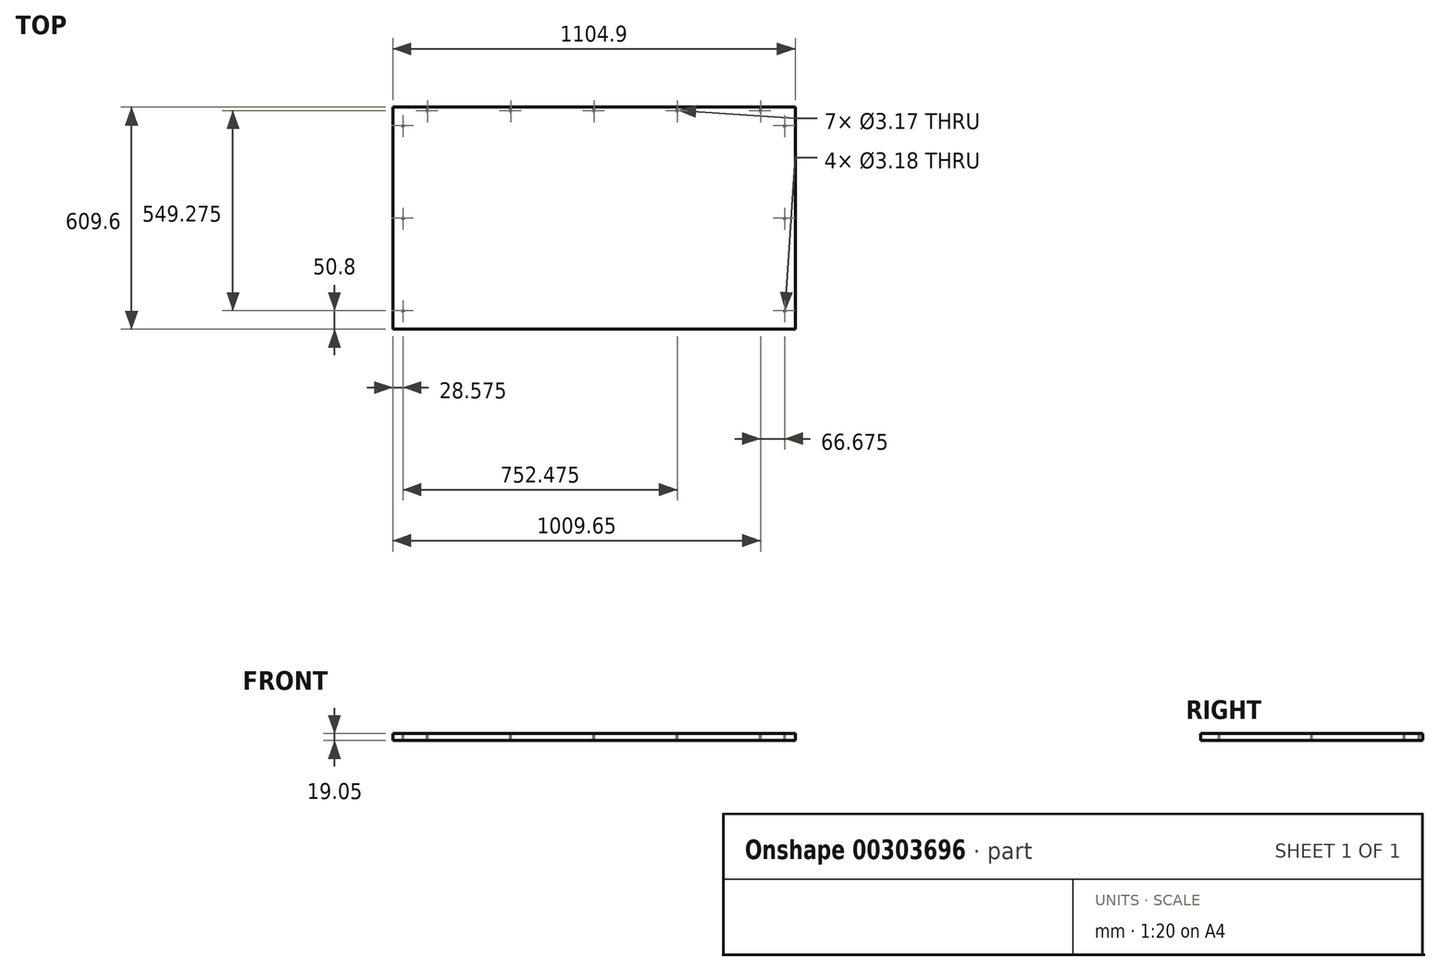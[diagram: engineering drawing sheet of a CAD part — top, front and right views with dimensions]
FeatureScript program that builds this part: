
annotation { "Feature Type Name" : "Feature", "Feature Type Description" : "" }
export const myFeature = defineFeature(function(context is Context, id is Id, definition is map)
    precondition{}
    {
        {
            var Q0;
            Q0=qCreatedBy(makeId("Top.planeOp"),FACE);
            var sketch = newSketch(context, id + "F0", { "sketchPlane" : qUnion([Q0])});
            skLineSegment(sketch, "E0.bottom", {"start": v(0, 0) * mm, "end": v(1104.9, 0) * mm});
            skLineSegment(sketch, "E0.top", {"start": v(0, -609.6) * mm, "end": v(1104.9, -609.6) * mm});
            skLineSegment(sketch, "E0.left", {"start": v(0, 0) * mm, "end": v(0, -609.6) * mm});
            skLineSegment(sketch, "E0.right", {"start": v(1104.9, 0) * mm, "end": v(1104.9, -609.6) * mm});
            skSolve(sketch);
        }
        {
            var Q0;
            Q0=makeQuery(id+"F0.imprint","IMPRINT",FACE,{"disambiguationData":[TD([[makeQuery(id+"F0.imprint","IMPRINT",EDGE,{"derivedFrom":sQuery(id+"F0.wireOp",EDGE,"E0.bottom")}),-1.0]])]});
            extrude(context, id + "F1", {"entities" : qUnion([Q0]), "oppositeDirection" : true, "depth" : 19.05 * mm});
        }
        {
            var Q0;
            Q0=qCreatedBy(makeId("Top.planeOp"),FACE);
            var sketch = newSketch(context, id + "F2", { "sketchPlane" : qUnion([Q0])});
            skCircle(sketch, "E1", {"center": v(95.25, -9.53) * mm, "radius": 1.59 * mm});
            skCircle(sketch, "E2.1.0.0", {"center": v(323.85, -9.52) * mm, "radius": 1.59 * mm});
            skCircle(sketch, "E2.2.0.0", {"center": v(552.45, -9.52) * mm, "radius": 1.59 * mm});
            skCircle(sketch, "E2.3.0.0", {"center": v(781.05, -9.52) * mm, "radius": 1.59 * mm});
            skCircle(sketch, "E2.4.0.0", {"center": v(1009.65, -9.52) * mm, "radius": 1.59 * mm});
            skLineSegment(sketch, "E2.direction1", {"start": v(95.25, -9.52) * mm, "end": v(323.85, -9.52) * mm, "construction": true});
            skSolve(sketch);
        }
        {
            var Q0;
            Q0 = qSketchRegion(id + "F2", true);
            extrude(context, id + "F3", {"entities" : qUnion([Q0]), "operationType" : NewBodyOperationType.REMOVE, "endBound" : BoundingType.THROUGH_ALL, "oppositeDirection" : true, "depth" : 25.4 * mm, "offsetDistance" : 25.4 * mm});
        }
        {
            var Q0;
            Q0=qCreatedBy(makeId("Top.planeOp"),FACE);
            var sketch = newSketch(context, id + "F4", { "sketchPlane" : qUnion([Q0])});
            skCircle(sketch, "E3", {"center": v(28.58, -50.8) * mm, "radius": 1.59 * mm});
            skCircle(sketch, "E4.0.1.0", {"center": v(28.58, -304.8) * mm, "radius": 1.59 * mm});
            skCircle(sketch, "E4.0.2.0", {"center": v(28.58, -558.8) * mm, "radius": 1.59 * mm});
            skCircle(sketch, "E4.1.0.0", {"center": v(1076.33, -50.8) * mm, "radius": 1.59 * mm});
            skCircle(sketch, "E4.1.1.0", {"center": v(1076.33, -304.8) * mm, "radius": 1.59 * mm});
            skCircle(sketch, "E4.1.2.0", {"center": v(1076.33, -558.8) * mm, "radius": 1.59 * mm});
            skLineSegment(sketch, "E4.direction1", {"start": v(28.58, -50.8) * mm, "end": v(1076.33, -50.8) * mm, "construction": true});
            skLineSegment(sketch, "E4.direction2", {"start": v(28.58, -50.8) * mm, "end": v(28.58, -304.8) * mm, "construction": true});
            skSolve(sketch);
        }
        {
            var Q0;
            Q0 = qSketchRegion(id + "F4", true);
            extrude(context, id + "F5", {"entities" : qUnion([Q0]), "operationType" : NewBodyOperationType.REMOVE, "endBound" : BoundingType.THROUGH_ALL, "oppositeDirection" : true, "depth" : 25.4 * mm, "offsetDistance" : 25.4 * mm});
        }
    });
